# Revit family: Deca_Acabamento para Registro de Pressão Disco_4916.C.DSC.PQ
name_source: partatom
category: Plumbing Fixtures
revit_build: Autodesk Revit Architecture 2012 (Build: 20110916_2132(x64)
units: mm (PartAtom-declared; Revit-internal decimal feet)

## types (9) — shared parameters
Acabamento = Deca CR10 Cromado Metal
Aprovado por = Contino/quattroD
Assembly Code = D2020
Atendimento ao Cliente = 0800-0117073
Consumo = Varia com a pressão
Criado por = Contino/quattroD
Código = 4916.C.DSC.PQ
Description = Acabamento para registro de pressão Axis
Flow Pressure = 0.00 psi
Informações Complementares = Mecanismo: 1/2 de volta
Linha = Disco
Louça/Metais = Metal
Manufacturer = Deca
Material = Deca_Latão Cromado e Plástico de Engenharia
Model = 4916.C.DSC.PQ
Norma = ABNT NBR 10283: 2003
Peso Liquido (Kg) = 0.21
Pressão = 2 A 40 mca
Produto = Acabamento para registro de pressão Disco
Segmento = Médio
URL = www.deca.com.br/produtos
Variações de COR = Cromado 1/2 e 3/4 (4916.C.DSC.PQ)
zero-valued in all types: CWFU, Default Elevation

## per-type parameters (varying)
| type | Base de Registro de Pressão_Family | Diâmetro Ponto de Agua | Raio Ponto de Agua |
| 4916.C.DSC.PQ_Cromado CR10_1/2" | Deca_Shared_Base de Registro de Pressão_4916.C.DSC.PQ : 4416.102 - DN 15 (1/2") | 15 mm  [stored 0.0492126 ft] | 8 mm  [stored 0.0262467 ft] |
| 4916.C.DSC.PQ_Cromado CR10_3/4" | Deca_Shared_Base de Registro de Pressão_4916.C.DSC.PQ : 4416.202 - DN 20 (3/4") | 20 mm  [stored 0.0656168 ft] | 10 mm  [stored 0.0328084 ft] |
| Base Fácil PVC 20mm (4416.102.PVC) | Deca_Shared_Base de Registro de Pressão_4916.C.DSC.PQ : 4416.202 - DN 20 (3/4") | 20 mm  [stored 0.0656168 ft] | 10 mm  [stored 0.0328084 ft] |
| Base Fácil PVC 25mm (4416.202.PVC) | Deca_Shared_Base de Registro de Pressão_4916.C.DSC.PQ : 4416.202 - DN 20 (3/4") | 25 mm  [stored 0.082021 ft] | 13 mm |
| Base Fácil PPR 20mm (4416.102.PPR) | Deca_Shared_Base de Registro de Pressão_4916.C.DSC.PQ : 4416.202 - DN 20 (3/4") | 20 mm  [stored 0.0656168 ft] | 10 mm  [stored 0.0328084 ft] |
| Base Fácil PPR 25mm (4416.202.PPR) | Deca_Shared_Base de Registro de Pressão_4916.C.DSC.PQ : 4416.202 - DN 20 (3/4") | 25 mm  [stored 0.082021 ft] | 13 mm |
| Base Fácil CPVC 15mm (4416.102.CPVC) | Deca_Shared_Base de Registro de Pressão_4916.C.DSC.PQ : 4416.202 - DN 20 (3/4") | 15 mm  [stored 0.0492126 ft] | 8 mm  [stored 0.0262467 ft] |
| Base Fácil CPVC 22mm (4416.202.CPVC) | Deca_Shared_Base de Registro de Pressão_4916.C.DSC.PQ : 4416.202 - DN 20 (3/4") | 22 mm  [stored 0.0721785 ft] | 11 mm  [stored 0.0360892 ft] |
| Base Fácil CPVC 28mm (4416.302.CPVC) | Deca_Shared_Base de Registro de Pressão_4916.C.DSC.PQ : 4416.202 - DN 20 (3/4") | 28 mm  [stored 0.0918635 ft] | 14 mm  [stored 0.0459318 ft] |

note: [stored X ft] marks values corroborated as IEEE doubles in the binary element streams (Revit-internal decimal feet)

## geometry (parser evidence)
native form markers: Blend x4, Sweep x4
no freeform markers — native parametric forms only
